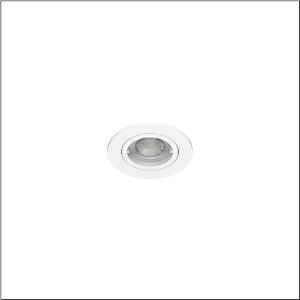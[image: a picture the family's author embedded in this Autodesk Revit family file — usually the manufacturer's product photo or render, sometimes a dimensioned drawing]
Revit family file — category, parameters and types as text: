
# Revit family: lunis_41_spot_51dt137a32a
name_source: partatom
category: Lighting Fixtures
units: mm (PartAtom-declared; Revit-internal decimal feet)

## family parameters
Cut with Voids When Loaded = No
Host = Face
Light Source = No
Part Type = Normal
Room Calculation Point = No
Round Connector Dimension = Use Diameter
Shared = No

## types (1)
- Lunis 41 Spot (1 x LED, 650 lm, 6.5 W, 3000K)
    Apparent Load = 7 VA
    CIE Flux Codes = 87 97 99 100 100
    Color Rendering = 80
    Color Temperature = 3000K
    Default Elevation = 1800 mm
    Description = Lunis 41,  Spot, downlight, light emission: direct distribution, LED rated luminous flux: 650lm, light colour: 830, control gear: ECG, mains connection: 230V, AC, 50/60Hz, housing, round, of aluminium, coated, traffic white (RAL 9016), diameter: 88mm, recess depth: 54mm, protection rating (complete): IP20, protection rating (on room side): IP20, insulation class (complete): insulation class II (safety insulation), certification: CE, permissible ambient temperature for indoor applications: -20..+40°C, packaging unit: 1 piece
    Height = 0 mm  [stored 0 ft]
    Lamp = 1 x LED
    Lamp Light Flux = 650 lm
    Lamp Power = 6.5 W
    Lamp count = 1
    Length = 88 mm
    Luminous efficacy = 100 lm/W
    Manufacturer = Siteco
    ModVariant = No
    Model = 51DT137A32A
    Mounting Place = Ceiling
    Mounting Type = Recessed
    Number of Poles = 1
    OnlyDefault = Yes
    Power Factor = 1
    Product Name = Lunis 41 Spot
    Product group = downlight
    ProductGroupID = 400
    Protection Class = Protection class II
    Protection Degree = IP 20
    RLX_Detail_Level = 1
    RLX_Emergency_Light_Flux = 0 lm
    RLX_Emergency_Type = 0
    RLX_Emergency_Type_DB = No
    RlxData = <blob elided: 38109 chars, md5=dc071232>
    Socket = socket
    Standby Power = 0 W
    System Light Flux = 650 lm
    System Power = 7 W
    Type Comments = Product without accessories
    Type Image = l_1005286.jpg
    URL = http://relux.com
    VarID = ---
    Voltage = 0 V
    Weight = 0.00 kg
    Width = 0 mm  [stored 0 ft]

note: [stored X ft] marks values corroborated as IEEE doubles in the binary element streams (Revit-internal decimal feet)

## geometry (parser evidence)
native form markers: Blend x4, Sweep x9
no freeform markers — native parametric forms only
